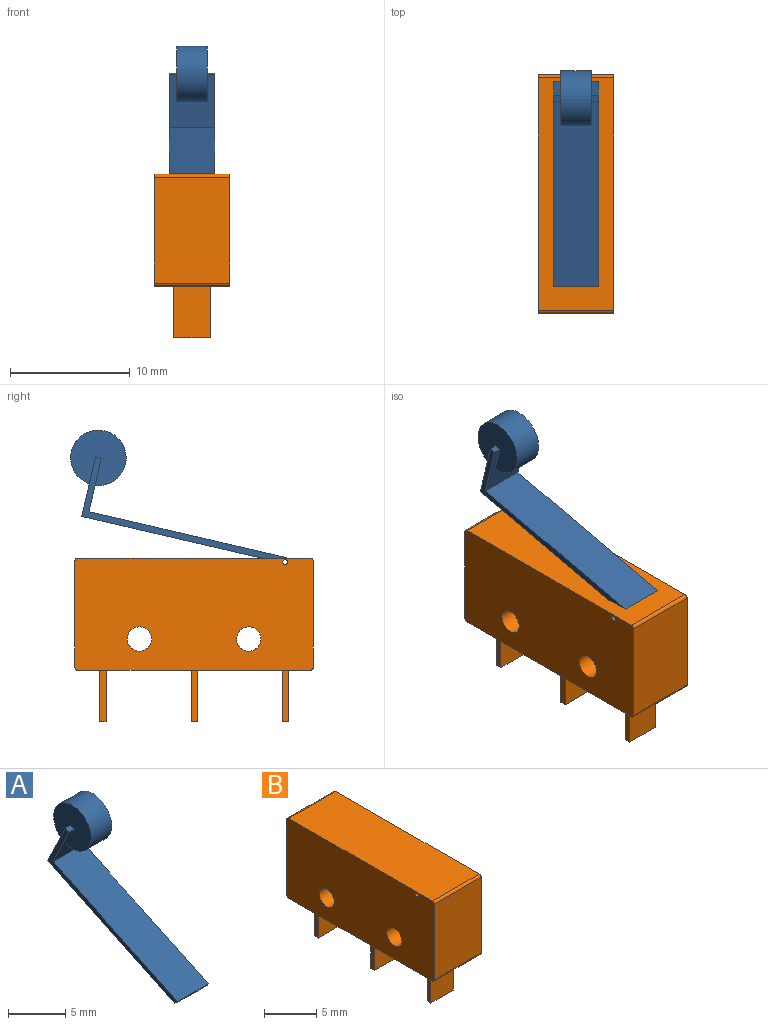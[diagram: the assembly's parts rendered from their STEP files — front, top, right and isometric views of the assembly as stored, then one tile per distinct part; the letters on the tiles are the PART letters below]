
ASSEMBLY  parts=2 mates=1
PART A: 13 faces, bbox 3.8x16x14.2 mm
  f0: plane 0.64x0.46mm, normal (0,-0.43,0.9), area 0.3mm2, adj f4,f6,f8,f11
  f1: plane 15.35x7.29mm, normal (0,-0.43,0.9), area 64.7mm2, adj f2,f6,f7,f8
  f2: plane 3.81x0.18mm, normal (0,-0.9,-0.43), area 0.8mm2, adj f1,f7,f8,f12
  f3: plane 15.6x7.41mm, normal (0,0.43,-0.9), area 65.8mm2, adj f4,f7,f8,f12
  f4: plane 4.59x3.81mm, normal (0,0.9,0.43), area 13.5mm2, adj f0,f3,f5,f7,f8,f9,f10,f11
  f5: plane 0.64x0.46mm, normal (0,-0.43,0.9), area 0.3mm2, adj f4,f6,f7,f10
  f6: plane 4.13x3.81mm, normal (0,-0.9,-0.43), area 11.6mm2, adj f0,f1,f5,f7,f8,f9,f10,f11
  f7: plane 16.03x12mm, normal (1,0,0), area 11.1mm2, adj f1,f2,f3,f4,f5,f6,f12
  f8: plane 16.03x12mm, normal (-1,0,0), area 11.1mm2, adj f0,f1,f2,f3,f4,f6,f12
  f9: cylinder r=2.32mm len=4.64mm, axis (-1,0,0), area 35.7mm2, adj f4,f6,f10,f11
  f10: plane 4.64x4.64mm, normal (1,0,0), area 15.7mm2, adj f4,f5,f6,f9
  f11: plane 4.64x4.64mm, normal (-1,0,0), area 15.7mm2, adj f0,f4,f6,f9
  f12: cylinder r=0.2mm len=3.81mm, axis (1,0,0), area 1.9mm2, adj f2,f3,f7,f8
PART B: 28 faces, bbox 6.4x19.9x13.7 mm
  f0: plane 4.32x0.51mm, normal (-1,0,0), area 2.2mm2, adj f1,f3,f4,f16
  f1: plane 4.32x3.05mm, normal (0,1,0), area 13.2mm2, adj f0,f2,f4,f16
  f2: plane 4.32x0.51mm, normal (1,0,0), area 2.2mm2, adj f1,f3,f4,f16
  f3: plane 4.32x3.05mm, normal (0,-1,0), area 13.2mm2, adj f0,f2,f4,f16
  f4: plane 3.05x0.51mm, normal (0,0,-1), area 1.5mm2, adj f0,f1,f2,f3
  f5: plane 4.32x0.51mm, normal (-1,0,0), area 2.2mm2, adj f6,f8,f9,f16
  f6: plane 4.32x3.05mm, normal (0,1,0), area 13.2mm2, adj f5,f7,f9,f16
  f7: plane 4.32x0.51mm, normal (1,0,0), area 2.2mm2, adj f6,f8,f9,f16
  f8: plane 4.32x3.05mm, normal (0,-1,0), area 13.2mm2, adj f5,f7,f9,f16
  f9: plane 3.05x0.51mm, normal (0,0,-1), area 1.5mm2, adj f5,f6,f7,f8
  f10: plane 8.86x6.35mm, normal (0,1,0), area 56.3mm2, adj f11,f19,f20,f21
  f11: cylinder r=0.25mm len=6.35mm, axis (-1,0,0), area 2.5mm2, adj f10,f12,f20,f21
  f12: plane 19.43x6.35mm, normal (0,0,1), area 123.4mm2, adj f11,f13,f20,f21
  f13: cylinder r=0.25mm len=6.35mm, axis (-1,0,0), area 2.5mm2, adj f12,f14,f20,f21
  f14: plane 8.86x6.35mm, normal (0,-1,0), area 56.3mm2, adj f13,f15,f20,f21
  f15: cylinder r=0.25mm len=6.35mm, axis (-1,0,0), area 2.5mm2, adj f14,f16,f20,f21
  f16: plane 19.43x6.35mm, normal (0,0,-1), area 118.7mm2, adj f0,f1,f2,f3,f5,f6,f7,f8
  f17: cylinder r=1.02mm len=6.35mm, axis (-1,0,0), area 40.7mm2, adj f20,f21
  f18: cylinder r=1.02mm len=6.35mm, axis (-1,0,0), area 40.7mm2, adj f20,f21
  f19: cylinder r=0.25mm len=6.35mm, axis (-1,0,0), area 2.5mm2, adj f10,f16,f20,f21
  f20: plane 19.94x9.37mm, normal (1,0,0), area 180.1mm2, adj f10,f11,f12,f13,f14,f15,f16,f17
  f21: plane 19.94x9.37mm, normal (-1,0,0), area 180.1mm2, adj f10,f11,f12,f13,f14,f15,f16,f17
  f22: plane 4.32x0.51mm, normal (-1,0,0), area 2.2mm2, adj f16,f23,f25,f26
  f23: plane 4.32x3.05mm, normal (0,1,0), area 13.2mm2, adj f16,f22,f24,f26
  f24: plane 4.32x0.51mm, normal (1,0,0), area 2.2mm2, adj f16,f23,f25,f26
  f25: plane 4.32x3.05mm, normal (0,-1,0), area 13.2mm2, adj f16,f22,f24,f26
  f26: plane 3.05x0.51mm, normal (0,0,-1), area 1.5mm2, adj f22,f23,f24,f25
  f27: cylinder r=0.2mm len=6.35mm, axis (1,0,0), area 8.1mm2, adj f20,f21
PLACE A rot(axis=(-1,0,0),12.4deg) t=(-0.93,-2.78,-8.15)mm
PLACE B t=(-0.93,-1.67,-6.62)mm fixed
MATE revolute A.f12 <-> B.f27  axis (1,0,0) through (0.97,-9.29,-2.27)mm
